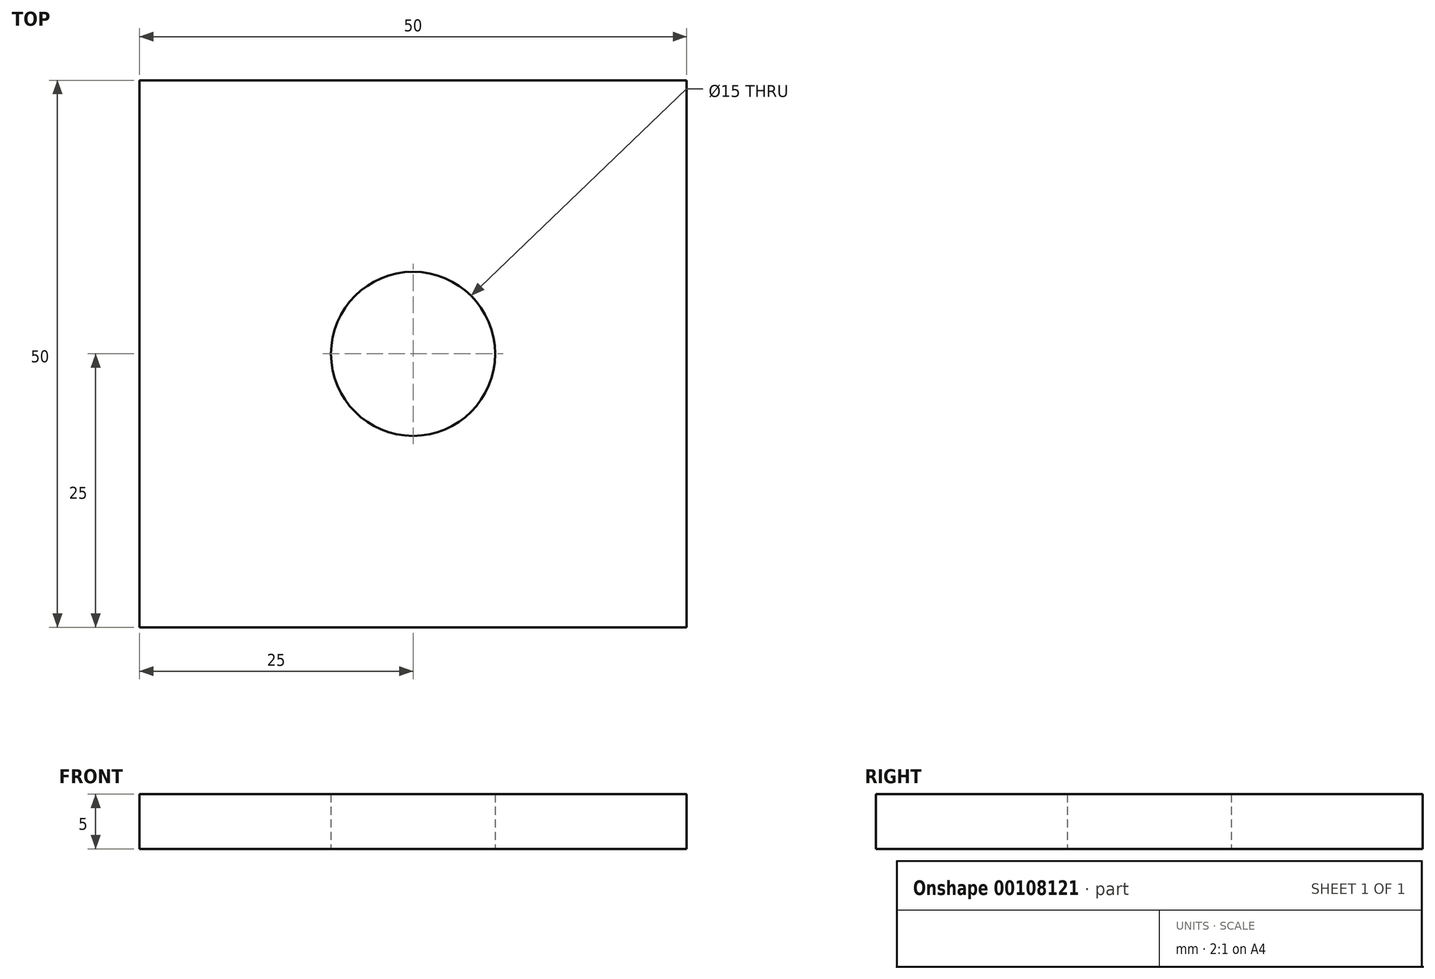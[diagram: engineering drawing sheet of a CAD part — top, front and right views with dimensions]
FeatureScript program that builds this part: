
annotation { "Feature Type Name" : "Feature", "Feature Type Description" : "" }
export const myFeature = defineFeature(function(context is Context, id is Id, definition is map)
    precondition{}
    {
        {
            var Q0;
            Q0=qCreatedBy(makeId("Top.planeOp"),FACE);
            var sketch = newSketch(context, id + "F0", { "sketchPlane" : qUnion([Q0])});
            skLineSegment(sketch, "E0.bottom", {"start": v(25, -25) * mm, "end": v(-25, -25) * mm});
            skLineSegment(sketch, "E0.top", {"start": v(25, 25) * mm, "end": v(-25, 25) * mm});
            skLineSegment(sketch, "E0.left", {"start": v(25, -25) * mm, "end": v(25, 25) * mm});
            skLineSegment(sketch, "E0.right", {"start": v(-25, -25) * mm, "end": v(-25, 25) * mm});
            skPoint(sketch, "E0.middle", {"position": v(0, 0) * mm});
            skCircle(sketch, "E1", {"center": v(0, 0) * mm, "radius": 7.5 * mm});
            skSolve(sketch);
        }
        {
            var Q0;
            Q0=makeQuery(id+"F0.imprint","IMPRINT",FACE,{"disambiguationData":[TD([[makeQuery(id+"F0.imprint","IMPRINT",EDGE,{"derivedFrom":sQuery(id+"F0.wireOp",EDGE,"E0.bottom")}),-1.0]])]});
            extrude(context, id + "F1", {"entities" : qUnion([Q0]), "depth" : 5 * mm});
        }
    });
